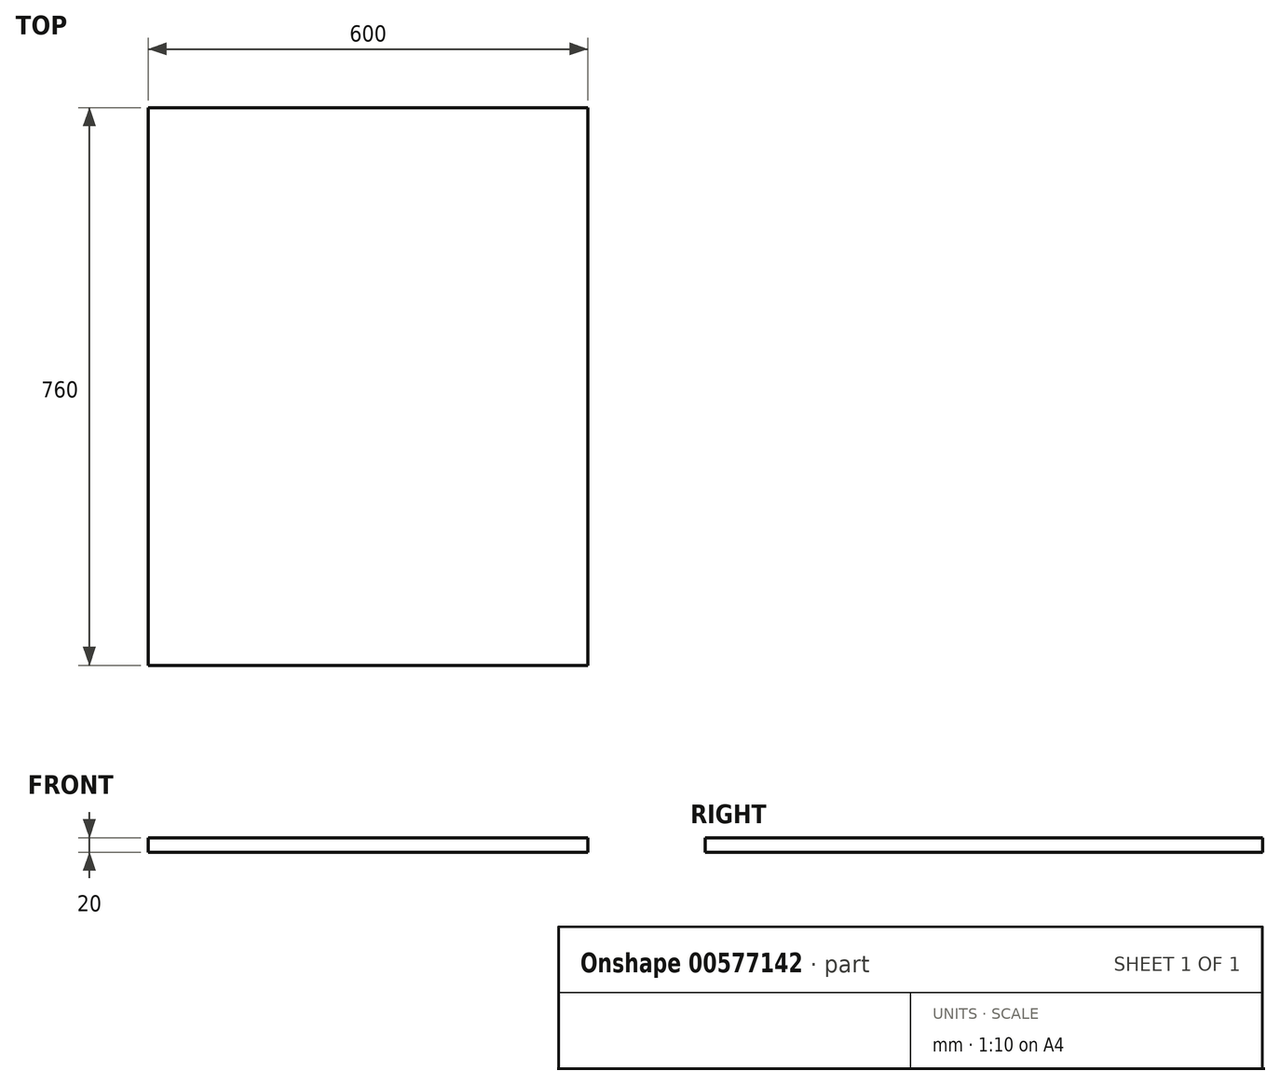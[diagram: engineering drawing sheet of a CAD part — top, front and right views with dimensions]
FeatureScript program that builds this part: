
annotation { "Feature Type Name" : "Feature", "Feature Type Description" : "" }
export const myFeature = defineFeature(function(context is Context, id is Id, definition is map)
    precondition{}
    {
        {
            var Q0;
            Q0=qCreatedBy(makeId("Top.planeOp"),FACE);
            var sketch = newSketch(context, id + "F0", { "sketchPlane" : qUnion([Q0])});
            skLineSegment(sketch, "E0.bottom", {"start": v(-291.15, 152.18) * mm, "end": v(308.85, 152.18) * mm});
            skLineSegment(sketch, "E0.top", {"start": v(-291.15, -607.82) * mm, "end": v(308.85, -607.82) * mm});
            skLineSegment(sketch, "E0.left", {"start": v(-291.15, 152.18) * mm, "end": v(-291.15, -607.82) * mm});
            skLineSegment(sketch, "E0.right", {"start": v(308.85, 152.18) * mm, "end": v(308.85, -607.82) * mm});
            skSolve(sketch);
        }
        {
            var Q0;
            Q0 = qSketchRegion(id + "F0", true);
            extrude(context, id + "F1", {"entities" : qUnion([Q0]), "depth" : 20 * mm, "offsetDistance" : 25 * mm});
        }
    });
